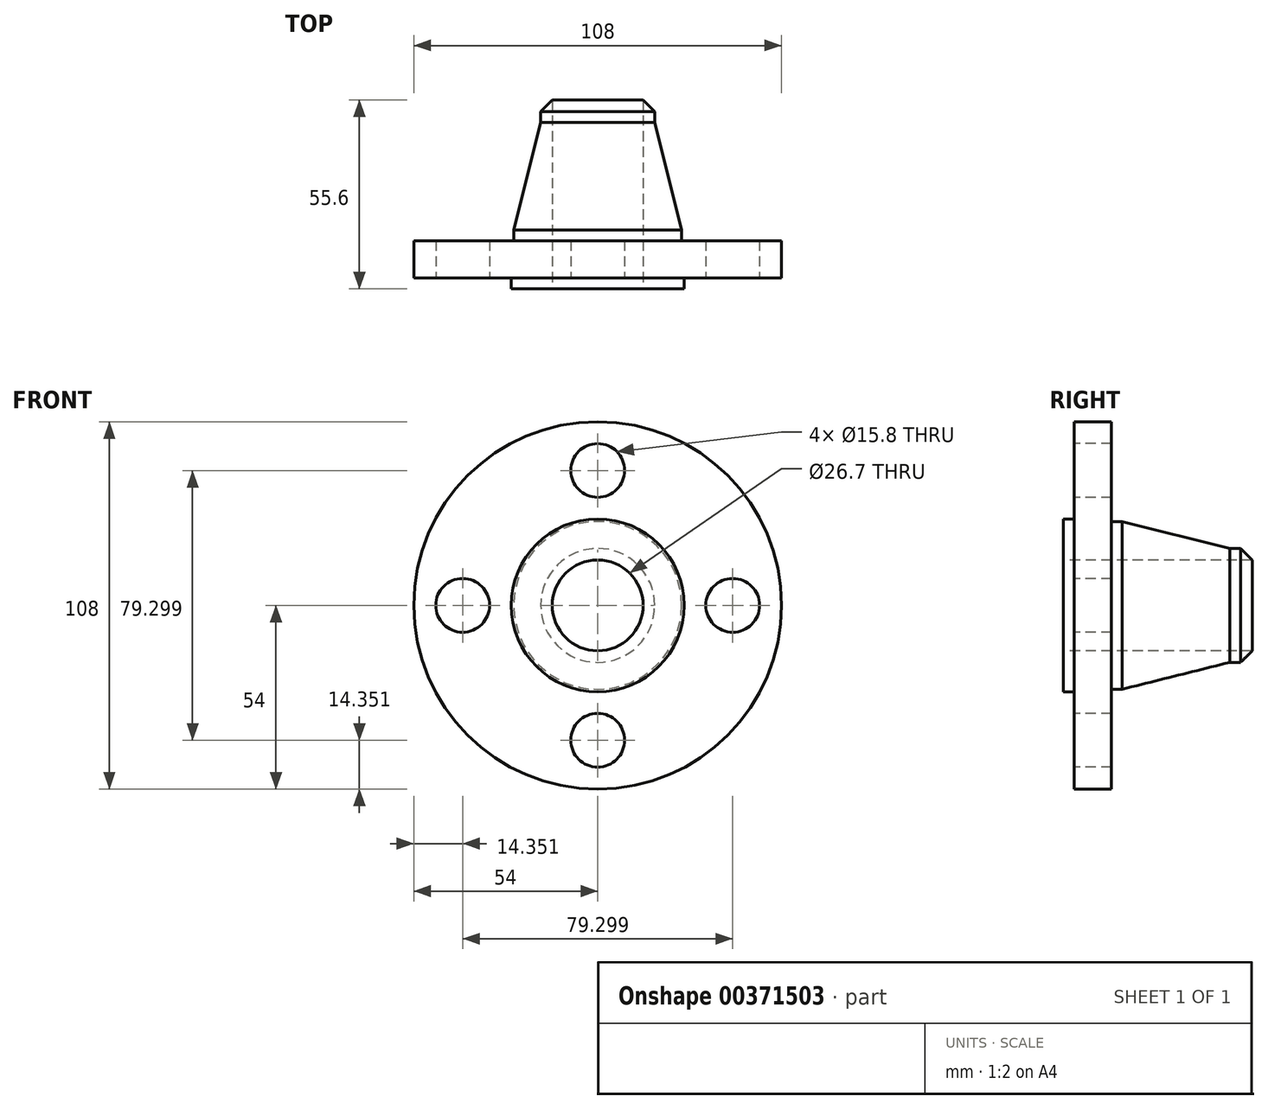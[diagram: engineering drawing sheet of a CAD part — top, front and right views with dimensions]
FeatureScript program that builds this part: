
annotation { "Feature Type Name" : "Feature", "Feature Type Description" : "" }
export const myFeature = defineFeature(function(context is Context, id is Id, definition is map)
    precondition{}
    {
        {
            var Q0;
            Q0=qCreatedBy(makeId("Right.planeOp"),FACE);
            var sketch = newSketch(context, id + "F0", { "sketchPlane" : qUnion([Q0])});
            skLineSegment(sketch, "E0", {"start": v(-75.38, 0) * mm, "end": v(74.52, 0) * mm, "construction": true});
            skLineSegment(sketch, "E1", {"start": v(0, 13.35) * mm, "end": v(0, 25.4) * mm});
            skLineSegment(sketch, "E2", {"start": v(0, 25.4) * mm, "end": v(3.17, 25.4) * mm});
            skLineSegment(sketch, "E3", {"start": v(3.17, 25.4) * mm, "end": v(3.17, 54) * mm});
            skLineSegment(sketch, "E4", {"start": v(3.17, 54) * mm, "end": v(14.2, 54) * mm});
            skLineSegment(sketch, "E5", {"start": v(14.2, 54) * mm, "end": v(14.2, 24.65) * mm});
            skLineSegment(sketch, "E6", {"start": v(14.2, 24.65) * mm, "end": v(17.37, 24.65) * mm});
            skLineSegment(sketch, "E7", {"start": v(55.6, 13.35) * mm, "end": v(0, 13.35) * mm});
            skLineSegment(sketch, "E8", {"start": v(17.37, 24.65) * mm, "end": v(48.94, 16.75) * mm});
            skLineSegment(sketch, "E9", {"start": v(48.94, 16.75) * mm, "end": v(52.12, 16.75) * mm});
            skLineSegment(sketch, "E10", {"start": v(52.12, 16.75) * mm, "end": v(55.6, 13.35) * mm});
            skSolve(sketch);
        }
        {
            var Q0;
            Q0=makeQuery(id+"F0.imprint","IMPRINT",FACE,{"disambiguationData":[TD([[makeQuery(id+"F0.imprint","IMPRINT",EDGE,{"derivedFrom":sQuery(id+"F0.wireOp",EDGE,"E1")}),-1.0]])]});
            var Q1;
            Q1=sQuery(id+"F0.wireOp",EDGE,"E0");
            revolve(context, id + "F1", {"entities" : qUnion([Q0]), "axis" : qUnion([Q1]), "revolveType" : RevolveType.FULL});
        }
        {
            var Q0;
            Q0=makeQuery(id+"F1.opRevolve","SWEPT_FACE",FACE,{"disambiguationData":[OSD([sQuery(id+"F0.wireOp",EDGE,"E3")])]});
            var sketch = newSketch(context, id + "F2", { "sketchPlane" : qUnion([Q0])});
            skLineSegment(sketch, "E11", {"start": v(0, 0) * mm, "end": v(0, 39.65) * mm, "construction": true});
            skCircle(sketch, "E12", {"center": v(0, 39.65) * mm, "radius": 7.9 * mm});
            skCircle(sketch, "E13.1.0", {"center": v(-39.65, 0) * mm, "radius": 7.9 * mm});
            skCircle(sketch, "E13.2.0", {"center": v(0, -39.65) * mm, "radius": 7.9 * mm});
            skCircle(sketch, "E13.3.0", {"center": v(39.65, 0) * mm, "radius": 7.9 * mm});
            skPoint(sketch, "E13.center", {"position": v(0, 0) * mm});
            skSolve(sketch);
        }
        {
            var Q0;
            Q0=makeQuery(id+"F2.imprint","IMPRINT",FACE,{"disambiguationData":[TD([[makeQuery(id+"F2.imprint","IMPRINT",EDGE,{"derivedFrom":sQuery(id+"F2.wireOp",EDGE,"E12")}),1.0]])]});
            var Q1;
            Q1=makeQuery(id+"F2.imprint","IMPRINT",FACE,{"disambiguationData":[TD([[makeQuery(id+"F2.imprint","IMPRINT",EDGE,{"derivedFrom":sQuery(id+"F2.wireOp",EDGE,"E13.1.0")}),1.0]])]});
            var Q2;
            Q2=makeQuery(id+"F2.imprint","IMPRINT",FACE,{"disambiguationData":[TD([[makeQuery(id+"F2.imprint","IMPRINT",EDGE,{"derivedFrom":sQuery(id+"F2.wireOp",EDGE,"E13.2.0")}),1.0]])]});
            var Q3;
            Q3=makeQuery(id+"F2.imprint","IMPRINT",FACE,{"disambiguationData":[TD([[makeQuery(id+"F2.imprint","IMPRINT",EDGE,{"derivedFrom":sQuery(id+"F2.wireOp",EDGE,"E13.3.0")}),1.0]])]});
            extrude(context, id + "F3", {"entities" : qUnion([Q0, Q1, Q2, Q3]), "operationType" : NewBodyOperationType.REMOVE, "endBound" : BoundingType.THROUGH_ALL, "oppositeDirection" : true, "depth" : 25.4 * mm});
        }
    });
